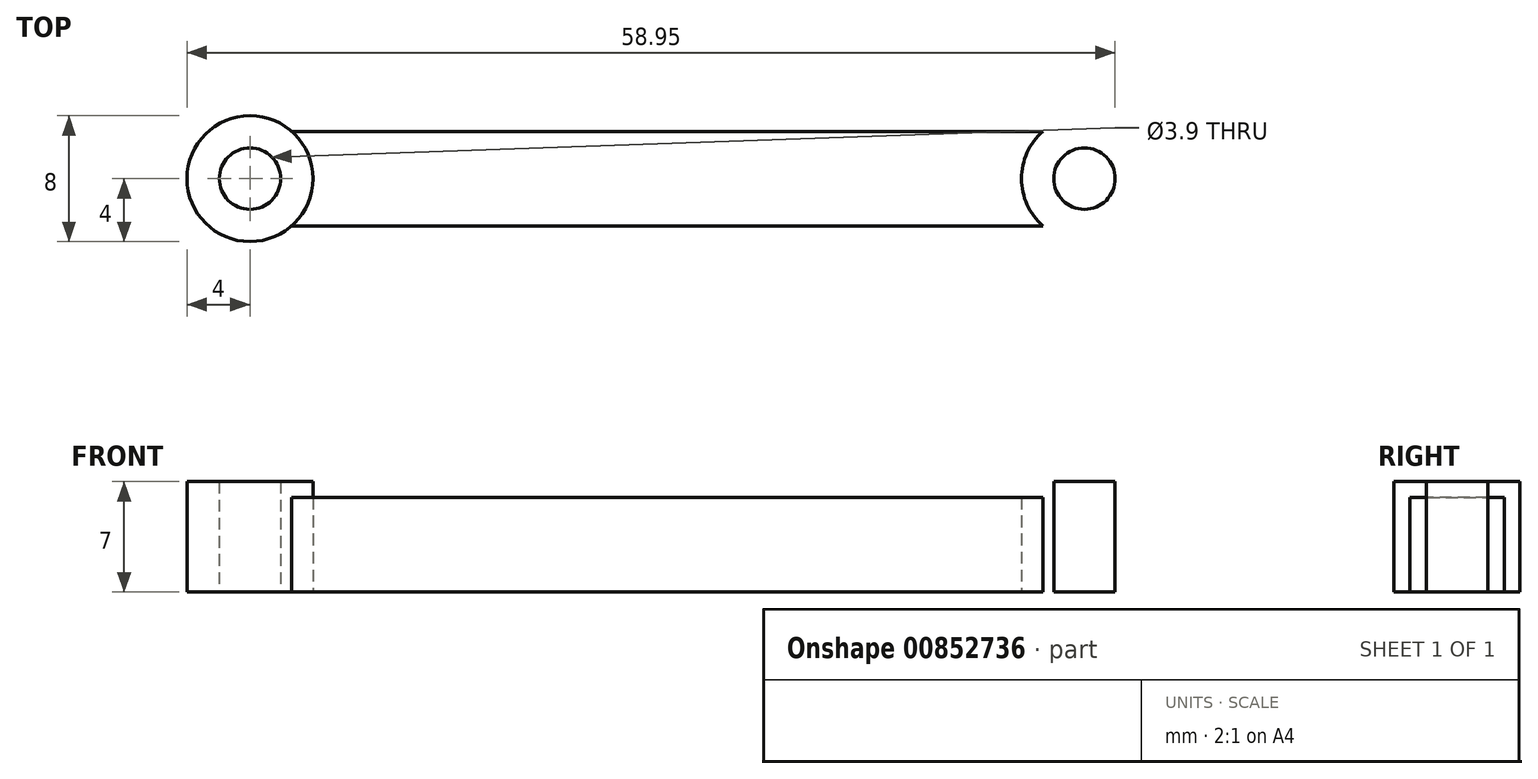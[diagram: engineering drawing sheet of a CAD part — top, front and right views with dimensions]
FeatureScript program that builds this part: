
annotation { "Feature Type Name" : "Feature", "Feature Type Description" : "" }
export const myFeature = defineFeature(function(context is Context, id is Id, definition is map)
    precondition{}
    {
        {
            var Q0;
            Q0=qCreatedBy(makeId("Top.planeOp"),FACE);
            var sketch = newSketch(context, id + "F0", { "sketchPlane" : qUnion([Q0])});
            skLineSegment(sketch, "E0", {"start": v(-26.5, 0) * mm, "end": v(26.5, 0) * mm, "construction": true});
            skCircle(sketch, "E1", {"center": v(-26.5, 0) * mm, "radius": 4 * mm});
            skCircle(sketch, "E2", {"center": v(26.5, 0) * mm, "radius": 4 * mm});
            skLineSegment(sketch, "E3", {"start": v(-23.85, 3) * mm, "end": v(23.85, 3) * mm});
            skLineSegment(sketch, "E4.MirrorCS", {"start": v(-23.85, -3) * mm, "end": v(23.85, -3) * mm});
            skCircle(sketch, "E5", {"center": v(-26.5, 0) * mm, "radius": 1.95 * mm});
            skCircle(sketch, "E6.MirrorC", {"center": v(26.5, 0) * mm, "radius": 1.95 * mm});
            skSolve(sketch);
        }
        {
            var Q0;
            Q0=makeQuery(id+"F0.imprint","IMPRINT",FACE,{"disambiguationData":[TD([[makeQuery(id+"F0.imprint","IMPRINT",EDGE,{"derivedFrom":sQuery(id+"F0.wireOp",EDGE,"E5")}),-1.0]])]});
            var Q1;
            Q1=makeQuery(id+"F0.imprint","IMPRINT",FACE,{"disambiguationData":[TD([[makeQuery(id+"F0.imprint","IMPRINT",EDGE,{"derivedFrom":sQuery(id+"F0.wireOp",EDGE,"E6.MirrorC")}),1.0]])]});
            extrude(context, id + "F1", {"entities" : qUnion([Q0, Q1]), "depth" : 7 * mm, "offsetDistance" : 25 * mm});
        }
        {
            var Q0;
            {var subQ0=sQuery(id+"F0.wireOp",EDGE,"E3");Q0=makeQuery(id+"F0.imprint","IMPRINT",FACE,{"disambiguationData":[TD([[makeQuery(id+"F0.imprint","IMPRINT",EDGE,{"derivedFrom":subQ0}),-1.0]])]});}
            extrude(context, id + "F2", {"entities" : qUnion([Q0]), "depth" : 6 * mm, "offsetDistance" : 25 * mm});
        }
    });
